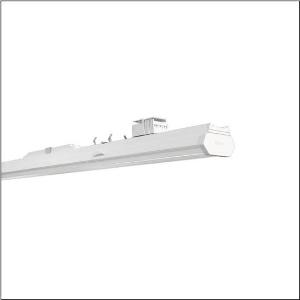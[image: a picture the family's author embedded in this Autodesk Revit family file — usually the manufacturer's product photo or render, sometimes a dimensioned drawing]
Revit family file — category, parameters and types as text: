
# Revit family: licross_r__11_protected_ho_51tp12dn4fxm3c_f4e0
name_source: partatom
category: Lighting Fixtures
units: mm (PartAtom-declared; Revit-internal decimal feet)

## family parameters
Cut with Voids When Loaded = No
Host = Face
Light Source = No
Part Type = Normal
Room Calculation Point = No
Round Connector Dimension = Use Diameter
Shared = No

## types (1)
- --- (1 x LED, 970 lm, 7.4 W, 4000K)
    Apparent Load = 7 VA
    CIE Flux Codes = 70 91 97 98 100
    Color Rendering = 80
    Color Temperature = 4000K
    Default Elevation = 1800 mm
    Description = Licross® 11 Protected HO, luminaire insert, of sheet steel, galvanised, coil coated, white, length: 1.500mm, width: 90mm, height: 101mm, LED rated luminous flux: 15.270lm, light colour: 840, control gear: DALI 2 (for two DALI lines), with plug, 6-pole, with phase selection, for trunking rail, 14-core, mains connection: 220..240V, AC, 50/60Hz, rated input power: 91W, for trunking rail, 14-core, halogen-free wiring, for emergency light function, converter,control gear: single battery element, battery: LiFePO4, 9Ah, primary light control with lens, of plastic, primary optical cover: cover, of PMMA, light emission: direct distribution, primary light characteristic: symmetric, protection rating (complete): IP64, insulation class (complete): insulation class I (protective earthing), certification: CE, UKCA, protection symbol: D if used in an environment with conductive dust loads with corresponding accessories, impact resistance: IK06, permissible ambient temperature for indoor applications: +5..+30°C, standard: EN 60598-2-22, LABS conformity tested according to VDMA 24364:2018-05, reducing of maximum allowable ambient temperature of 5°C with ceiling mounting, corresponds to IFS (International Featured Standards) requirements for safety and quality in the food industry, packaging unit: 1 piece
    Height = 92 mm
    Lamp = 1 x LED
    Lamp Light Flux = 970 lm
    Lamp Power = 7.4 W
    Lamp count = 1
    Length = 1500 mm
    Luminous efficacy = 131 lm/W
    Manufacturer = Siteco
    ModVariant = No
    Model = 51TP12DN4FXM3C
    Mounting Place = Ceiling
    Mounting Type = Pendant
    Number of Poles = 1
    OnlyDefault = Yes
    Power Factor = 1
    Product Name = Licross® 11 Protected HO
    Product group = luminaire insert
    ProductGroupID = 901
    Protection Class = Protection class I
    Protection Degree = IP 64
    RLX_Detail_Level = 1
    RLX_Emergency_Light_Flux = 0 lm
    RLX_Emergency_Type = 0
    RLX_Emergency_Type_DB = No
    RlxData = <blob elided: 24849 chars, md5=cacedb78>
    Socket = socket
    Standby Power = 0 W
    System Light Flux = 970 lm
    System Power = 7 W
    Type Comments = : emergency light operation: 3 h
    Type Image = l_1256148.jpg
    URL = http://relux.com
    VarID = @adj_059707
    Voltage = 0 V
    Weight = 0.00 kg
    Width = 88 mm

## geometry (parser evidence)
native form markers: Blend x4, Sweep x9
no freeform markers — native parametric forms only
